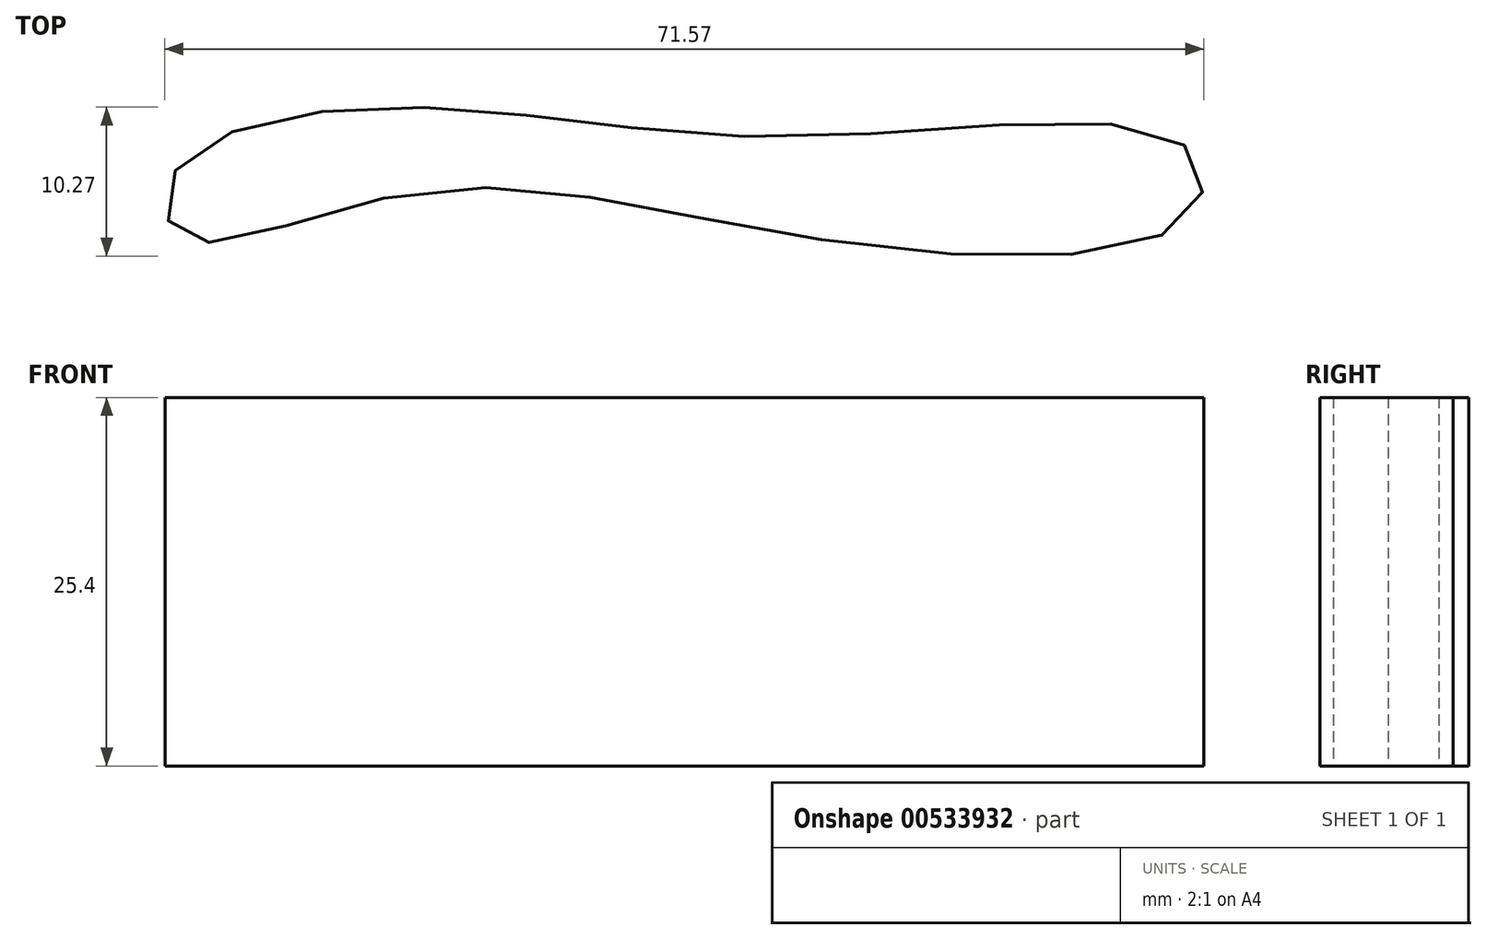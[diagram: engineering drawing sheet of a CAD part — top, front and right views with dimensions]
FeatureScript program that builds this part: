
annotation { "Feature Type Name" : "Feature", "Feature Type Description" : "" }
export const myFeature = defineFeature(function(context is Context, id is Id, definition is map)
    precondition{}
    {
        {
            var Q0;
            Q0=qCreatedBy(makeId("Top.planeOp"),FACE);
            var sketch = newSketch(context, id + "F0", { "sketchPlane" : qUnion([Q0])});
            skFitSpline(sketch, "E0", {"points": [v(-64.83, 7.98) * mm, v(-49.14, 12.35) * mm, v(-22.38, 10.3) * mm, v(4.63, 9.78) * mm, v(4.89, 4.63) * mm, v(-21.1, 3.34) * mm, v(-48.62, 6.43) * mm, v(-64.32, 3.34) * mm, v(-64.83, 7.98) * mm]});
            skSolve(sketch);
        }
        {
            var Q0;
            Q0 = qSketchRegion(id + "F0", true);
            extrude(context, id + "F1", {"entities" : qUnion([Q0]), "depth" : 25.4 * mm, "offsetDistance" : 25.4 * mm});
        }
    });
